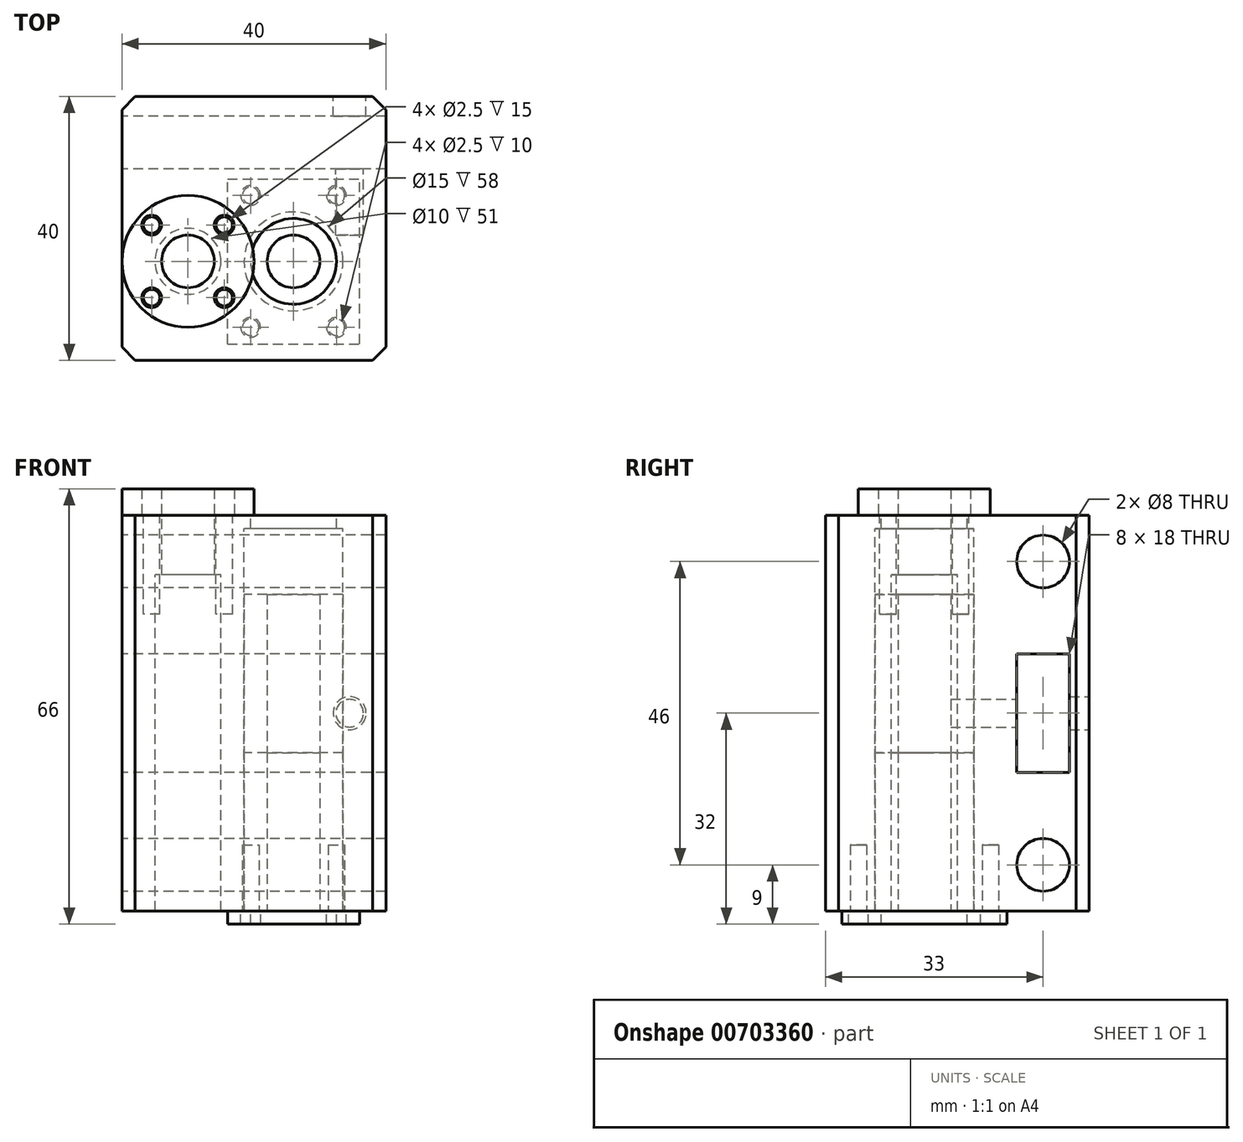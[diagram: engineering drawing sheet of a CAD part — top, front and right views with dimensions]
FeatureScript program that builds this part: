
annotation { "Feature Type Name" : "Feature", "Feature Type Description" : "" }
export const myFeature = defineFeature(function(context is Context, id is Id, definition is map)
    precondition{}
    {
        {
            var Q0;
            Q0=qCreatedBy(makeId("Top.planeOp"),FACE);
            var sketch = newSketch(context, id + "F0", { "sketchPlane" : qUnion([Q0])});
            skCircle(sketch, "E0", {"center": v(0, 0) * mm, "radius": 5 * mm});
            skCircle(sketch, "E1", {"center": v(0, 0) * mm, "radius": 10 * mm});
            skLineSegment(sketch, "E2.bottom", {"start": v(-5.5, 5.5) * mm, "end": v(5.5, 5.5) * mm, "construction": true});
            skLineSegment(sketch, "E2.top", {"start": v(-5.5, -5.5) * mm, "end": v(5.5, -5.5) * mm, "construction": true});
            skLineSegment(sketch, "E2.left", {"start": v(-5.5, 5.5) * mm, "end": v(-5.5, -5.5) * mm, "construction": true});
            skLineSegment(sketch, "E2.right", {"start": v(5.5, 5.5) * mm, "end": v(5.5, -5.5) * mm, "construction": true});
            skCircle(sketch, "E3", {"center": v(-5.5, 5.5) * mm, "radius": 1.5 * mm});
            skCircle(sketch, "E4", {"center": v(5.5, 5.5) * mm, "radius": 1.5 * mm});
            skCircle(sketch, "E5", {"center": v(5.5, -5.5) * mm, "radius": 1.5 * mm});
            skCircle(sketch, "E6", {"center": v(-5.5, -5.5) * mm, "radius": 1.5 * mm});
            skCircle(sketch, "E7", {"center": v(0, 0) * mm, "radius": 4 * mm});
            skCircle(sketch, "E8", {"center": v(-5.5, -5.5) * mm, "radius": 1.25 * mm});
            skCircle(sketch, "E9", {"center": v(-5.5, 5.5) * mm, "radius": 1.25 * mm});
            skCircle(sketch, "E10", {"center": v(5.5, -5.5) * mm, "radius": 1.25 * mm});
            skCircle(sketch, "E11", {"center": v(5.5, 5.5) * mm, "radius": 1.25 * mm});
            skSolve(sketch);
        }
        {
            var Q0;
            Q0 = qSketchRegion(id + "F0", true);
            var Q1;
            Q1=makeQuery(id+"F0.imprint","IMPRINT",FACE,{"disambiguationData":[TD([[makeQuery(id+"F0.imprint","IMPRINT",EDGE,{"derivedFrom":sQuery(id+"F0.wireOp",EDGE,"E0")}),1.0]])]});
            extrude(context, id + "F1", {"entities" : qUnion([Q0, Q1]), "depth" : 4 * mm, "offsetDistance" : 25 * mm});
        }
        {
            var Q0;
            Q0=makeQuery(id+"F0.imprint","IMPRINT",FACE,{"disambiguationData":[TD([[makeQuery(id+"F0.imprint","IMPRINT",EDGE,{"derivedFrom":sQuery(id+"F0.wireOp",EDGE,"E0")}),1.0]])]});
            extrude(context, id + "F2", {"entities" : qUnion([Q0]), "operationType" : NewBodyOperationType.ADD, "oppositeDirection" : true, "depth" : 9 * mm, "offsetDistance" : 25 * mm});
        }
        {
            var Q0;
            Q0=qCreatedBy(makeId("Top.planeOp"),FACE);
            var sketch = newSketch(context, id + "F3", { "sketchPlane" : qUnion([Q0])});
            skCircle(sketch, "E12", {"center": v(0, 0) * mm, "radius": 5 * mm});
            skCircle(sketch, "E13", {"center": v(16, 0) * mm, "radius": 7.5 * mm});
            skCircle(sketch, "E14", {"center": v(16, 0) * mm, "radius": 6.5 * mm});
            skLineSegment(sketch, "E15.bottom", {"start": v(-10, 25) * mm, "end": v(30, 25) * mm});
            skLineSegment(sketch, "E15.top", {"start": v(-10, -15) * mm, "end": v(30, -15) * mm});
            skLineSegment(sketch, "E15.left", {"start": v(-10, 25) * mm, "end": v(-10, -15) * mm});
            skLineSegment(sketch, "E15.right", {"start": v(30, 25) * mm, "end": v(30, -15) * mm});
            skSolve(sketch);
        }
        {
            var Q0;
            Q0 = qSketchRegion(id + "F3", true);
            extrude(context, id + "F4", {"entities" : qUnion([Q0]), "oppositeDirection" : true, "depth" : 60 * mm, "offsetDistance" : 25 * mm});
        }
        {
            var Q0;
            Q0=makeQuery(id+"F3.imprint","IMPRINT",FACE,{"disambiguationData":[TD([[makeQuery(id+"F3.imprint","IMPRINT",EDGE,{"derivedFrom":sQuery(id+"F3.wireOp",EDGE,"E13")}),1.0]])]});
            extrude(context, id + "F5", {"entities" : qUnion([Q0]), "operationType" : NewBodyOperationType.ADD, "oppositeDirection" : true, "depth" : 2 * mm, "offsetDistance" : 25 * mm});
        }
        {
            var Q0;
            Q0=makeQuery(id+"F4.opExtrude","SWEPT_FACE",FACE,{"disambiguationData":[OSD([sQuery(id+"F3.wireOp",EDGE,"E15.left")])]});
            var sketch = newSketch(context, id + "F6", { "sketchPlane" : qUnion([Q0])});
            skLineSegment(sketch, "E16", {"start": v(-18, 0) * mm, "end": v(-18, -60) * mm, "construction": true});
            skCircle(sketch, "E17", {"center": v(-18, -7) * mm, "radius": 4 * mm});
            skCircle(sketch, "E18", {"center": v(-18, -53) * mm, "radius": 4 * mm});
            skLineSegment(sketch, "E19.bottom", {"start": v(-22, -21) * mm, "end": v(-14, -21) * mm});
            skLineSegment(sketch, "E19.top", {"start": v(-22, -39) * mm, "end": v(-14, -39) * mm});
            skLineSegment(sketch, "E19.left", {"start": v(-22, -21) * mm, "end": v(-22, -39) * mm});
            skLineSegment(sketch, "E19.right", {"start": v(-14, -21) * mm, "end": v(-14, -39) * mm});
            skPoint(sketch, "E19.middle", {"position": v(-18, -30) * mm});
            skSolve(sketch);
        }
        {
            var Q0;
            Q0=makeQuery(id+"F6.imprint","IMPRINT",FACE,{"disambiguationData":[TD([[makeQuery(id+"F6.imprint","IMPRINT",EDGE,{"derivedFrom":sQuery(id+"F6.wireOp",EDGE,"E17")}),1.0]])]});
            var Q1;
            Q1=makeQuery(id+"F6.imprint","IMPRINT",FACE,{"disambiguationData":[TD([[makeQuery(id+"F6.imprint","IMPRINT",EDGE,{"derivedFrom":sQuery(id+"F6.wireOp",EDGE,"E19.bottom")}),-1.0]])]});
            var Q2;
            Q2=makeQuery(id+"F6.imprint","IMPRINT",FACE,{"disambiguationData":[TD([[makeQuery(id+"F6.imprint","IMPRINT",EDGE,{"derivedFrom":sQuery(id+"F6.wireOp",EDGE,"E18")}),1.0]])]});
            extrude(context, id + "F7", {"entities" : qUnion([Q0, Q1, Q2]), "operationType" : NewBodyOperationType.REMOVE, "oppositeDirection" : true, "depth" : 50 * mm, "offsetDistance" : 25 * mm});
        }
        {
            var Q0;
            Q0=makeQuery(id+"F0.imprint","IMPRINT",FACE,{"disambiguationData":[TD([[makeQuery(id+"F0.imprint","IMPRINT",EDGE,{"derivedFrom":sQuery(id+"F0.wireOp",EDGE,"E10")}),1.0]])]});
            var Q1;
            Q1=makeQuery(id+"F0.imprint","IMPRINT",FACE,{"disambiguationData":[TD([[makeQuery(id+"F0.imprint","IMPRINT",EDGE,{"derivedFrom":sQuery(id+"F0.wireOp",EDGE,"E8")}),1.0]])]});
            var Q2;
            Q2=makeQuery(id+"F0.imprint","IMPRINT",FACE,{"disambiguationData":[TD([[makeQuery(id+"F0.imprint","IMPRINT",EDGE,{"derivedFrom":sQuery(id+"F0.wireOp",EDGE,"E9")}),1.0]])]});
            var Q3;
            Q3=makeQuery(id+"F0.imprint","IMPRINT",FACE,{"disambiguationData":[TD([[makeQuery(id+"F0.imprint","IMPRINT",EDGE,{"derivedFrom":sQuery(id+"F0.wireOp",EDGE,"E11")}),1.0]])]});
            extrude(context, id + "F8", {"entities" : qUnion([Q0, Q1, Q2, Q3]), "operationType" : NewBodyOperationType.REMOVE, "oppositeDirection" : true, "depth" : 15 * mm, "offsetDistance" : 25 * mm});
        }
        {
            var Q0;
            Q0=makeQuery(id+"F4.opExtrude","SWEPT_FACE",FACE,{"disambiguationData":[OSD([sQuery(id+"F3.wireOp",EDGE,"E15.bottom")])]});
            var sketch = newSketch(context, id + "F9", { "sketchPlane" : qUnion([Q0])});
            skCircle(sketch, "E20", {"center": v(-24.5, -30) * mm, "radius": 2.1 * mm});
            skCircle(sketch, "E21", {"center": v(-24.5, -30) * mm, "radius": 2.5 * mm});
            skSolve(sketch);
        }
        {
            var Q0;
            Q0=makeQuery(id+"F9.imprint","IMPRINT",FACE,{"disambiguationData":[TD([[makeQuery(id+"F9.imprint","IMPRINT",EDGE,{"derivedFrom":sQuery(id+"F9.wireOp",EDGE,"E20")}),1.0]])]});
            extrude(context, id + "F10", {"entities" : qUnion([Q0]), "operationType" : NewBodyOperationType.REMOVE, "oppositeDirection" : true, "depth" : (13 + 8) * mm, "offsetDistance" : 25 * mm});
        }
        {
            var Q0;
            Q0 = qSketchRegion(id + "F9", true);
            extrude(context, id + "F11", {"entities" : qUnion([Q0]), "operationType" : NewBodyOperationType.REMOVE, "oppositeDirection" : true, "depth" : 5 * mm, "offsetDistance" : 25 * mm});
        }
        {
            var Q0;
            Q0=makeQuery(id+"F4.opExtrude","SWEPT_EDGE",EDGE,{"disambiguationData":[OSD([sQuery(id+"F3.wireOp",EDGE,"E15.top"),sQuery(id+"F3.wireOp",EDGE,"E15.left")])]});
            var Q1;
            Q1=makeQuery(id+"F4.opExtrude","SWEPT_EDGE",EDGE,{"disambiguationData":[OSD([sQuery(id+"F3.wireOp",EDGE,"E15.top"),sQuery(id+"F3.wireOp",EDGE,"E15.right")])]});
            var Q2;
            Q2=makeQuery(id+"F4.opExtrude","SWEPT_EDGE",EDGE,{"disambiguationData":[OSD([sQuery(id+"F3.wireOp",EDGE,"E15.bottom"),sQuery(id+"F3.wireOp",EDGE,"E15.right")])]});
            var Q3;
            Q3=makeQuery(id+"F4.opExtrude","SWEPT_EDGE",EDGE,{"disambiguationData":[OSD([sQuery(id+"F3.wireOp",EDGE,"E15.bottom"),sQuery(id+"F3.wireOp",EDGE,"E15.left")])]});
            chamfer(context, id + "F12", {"entities" : qUnion([Q0, Q1, Q2, Q3]), "width" : 2 * mm, "tangentPropagation" : true});
        }
        {
            var Q0;
            Q0=makeQuery(id+"F4.opExtrude","CAP_FACE",FACE,{"disambiguationData":[OSD([sQuery(id+"F3.wireOp",EDGE,"E12"),sQuery(id+"F3.wireOp",EDGE,"E13"),sQuery(id+"F3.wireOp",EDGE,"E15.bottom"),sQuery(id+"F3.wireOp",EDGE,"E15.top"),sQuery(id+"F3.wireOp",EDGE,"E15.left"),sQuery(id+"F3.wireOp",EDGE,"E15.right")])],"isStart":false});
            var sketch = newSketch(context, id + "F13", { "sketchPlane" : qUnion([Q0])});
            skCircle(sketch, "E22", {"center": v(16, 0) * mm, "radius": 7.5 * mm});
            skCircle(sketch, "E23", {"center": v(16, 0) * mm, "radius": 4 * mm});
            skLineSegment(sketch, "E24.bottom", {"start": v(6, 12.5) * mm, "end": v(26, 12.5) * mm});
            skLineSegment(sketch, "E24.top", {"start": v(6, -12.5) * mm, "end": v(26, -12.5) * mm});
            skLineSegment(sketch, "E24.left", {"start": v(6, 12.5) * mm, "end": v(6, -12.5) * mm});
            skLineSegment(sketch, "E24.right", {"start": v(26, 12.5) * mm, "end": v(26, -12.5) * mm});
            skLineSegment(sketch, "E25.bottom", {"start": v(9.5, 10) * mm, "end": v(22.5, 10) * mm, "construction": true});
            skLineSegment(sketch, "E25.top", {"start": v(9.5, -10) * mm, "end": v(22.5, -10) * mm, "construction": true});
            skLineSegment(sketch, "E25.left", {"start": v(9.5, 10) * mm, "end": v(9.5, -10) * mm, "construction": true});
            skLineSegment(sketch, "E25.right", {"start": v(22.5, 10) * mm, "end": v(22.5, -10) * mm, "construction": true});
            skCircle(sketch, "E26", {"center": v(9.5, 10) * mm, "radius": 1.5 * mm});
            skCircle(sketch, "E27", {"center": v(22.5, 10) * mm, "radius": 1.5 * mm});
            skCircle(sketch, "E28", {"center": v(22.5, -10) * mm, "radius": 1.5 * mm});
            skCircle(sketch, "E29", {"center": v(9.5, -10) * mm, "radius": 1.5 * mm});
            skCircle(sketch, "E30", {"center": v(9.5, -10) * mm, "radius": 1.25 * mm});
            skCircle(sketch, "E31", {"center": v(22.5, -10) * mm, "radius": 1.25 * mm});
            skCircle(sketch, "E32", {"center": v(22.5, 10) * mm, "radius": 1.25 * mm});
            skCircle(sketch, "E33", {"center": v(9.5, 10) * mm, "radius": 1.25 * mm});
            skCircle(sketch, "E34", {"center": v(16, 0) * mm, "radius": 6.5 * mm});
            skSolve(sketch);
        }
        {
            var Q0;
            Q0=makeQuery(id+"F13.imprint","IMPRINT",FACE,{"disambiguationData":[TD([[makeQuery(id+"F13.imprint","IMPRINT",EDGE,{"derivedFrom":sQuery(id+"F13.wireOp",EDGE,"E22")}),-1.0]])]});
            var Q1;
            Q1=makeQuery(id+"F13.imprint","IMPRINT",FACE,{"disambiguationData":[TD([[makeQuery(id+"F13.imprint","IMPRINT",EDGE,{"derivedFrom":sQuery(id+"F13.wireOp",EDGE,"E23")}),-1.0]])]});
            extrude(context, id + "F14", {"entities" : qUnion([Q0, Q1]), "oppositeDirection" : true, "depth" : 48 * mm, "offsetDistance" : 25 * mm, "hasSecondDirection" : true, "secondDirectionOppositeDirection" : true, "secondDirectionDepth" : 24 * mm});
        }
        {
            var Q0;
            Q0=makeQuery(id+"F13.imprint","IMPRINT",FACE,{"disambiguationData":[TD([[makeQuery(id+"F13.imprint","IMPRINT",EDGE,{"derivedFrom":sQuery(id+"F13.wireOp",EDGE,"E23")}),-1.0]])]});
            var Q1;
            Q1=makeQuery(id+"F13.imprint","IMPRINT",FACE,{"disambiguationData":[TD([[makeQuery(id+"F13.imprint","IMPRINT",EDGE,{"derivedFrom":sQuery(id+"F13.wireOp",EDGE,"E22")}),-1.0]])]});
            extrude(context, id + "F15", {"entities" : qUnion([Q0, Q1]), "oppositeDirection" : true, "depth" : 24 * mm, "offsetDistance" : 25 * mm});
        }
        {
            var Q0;
            Q0=makeQuery(id+"F13.imprint","IMPRINT",FACE,{"disambiguationData":[TD([[makeQuery(id+"F13.imprint","IMPRINT",EDGE,{"derivedFrom":sQuery(id+"F13.wireOp",EDGE,"E33")}),1.0]])]});
            var Q1;
            Q1=makeQuery(id+"F13.imprint","IMPRINT",FACE,{"disambiguationData":[TD([[makeQuery(id+"F13.imprint","IMPRINT",EDGE,{"derivedFrom":sQuery(id+"F13.wireOp",EDGE,"E32")}),1.0]])]});
            var Q2;
            Q2=makeQuery(id+"F13.imprint","IMPRINT",FACE,{"disambiguationData":[TD([[makeQuery(id+"F13.imprint","IMPRINT",EDGE,{"derivedFrom":sQuery(id+"F13.wireOp",EDGE,"E31")}),1.0]])]});
            var Q3;
            Q3=makeQuery(id+"F13.imprint","IMPRINT",FACE,{"disambiguationData":[TD([[makeQuery(id+"F13.imprint","IMPRINT",EDGE,{"derivedFrom":sQuery(id+"F13.wireOp",EDGE,"E30")}),1.0]])]});
            extrude(context, id + "F16", {"entities" : qUnion([Q0, Q1, Q2, Q3]), "operationType" : NewBodyOperationType.REMOVE, "oppositeDirection" : true, "depth" : 10 * mm, "offsetDistance" : 25 * mm});
        }
        {
            var Q0;
            Q0=makeQuery(id+"F13.imprint","IMPRINT",FACE,{"disambiguationData":[TD([[makeQuery(id+"F13.imprint","IMPRINT",EDGE,{"derivedFrom":sQuery(id+"F13.wireOp",EDGE,"E22")}),-1.0]])]});
            var Q1;
            Q1=makeQuery(id+"F13.imprint","IMPRINT",FACE,{"disambiguationData":[TD([[makeQuery(id+"F13.imprint","IMPRINT",EDGE,{"derivedFrom":sQuery(id+"F13.wireOp",EDGE,"E22")}),1.0]])]});
            extrude(context, id + "F17", {"entities" : qUnion([Q0, Q1]), "depth" : 2 * mm, "offsetDistance" : 25 * mm});
        }
    });
